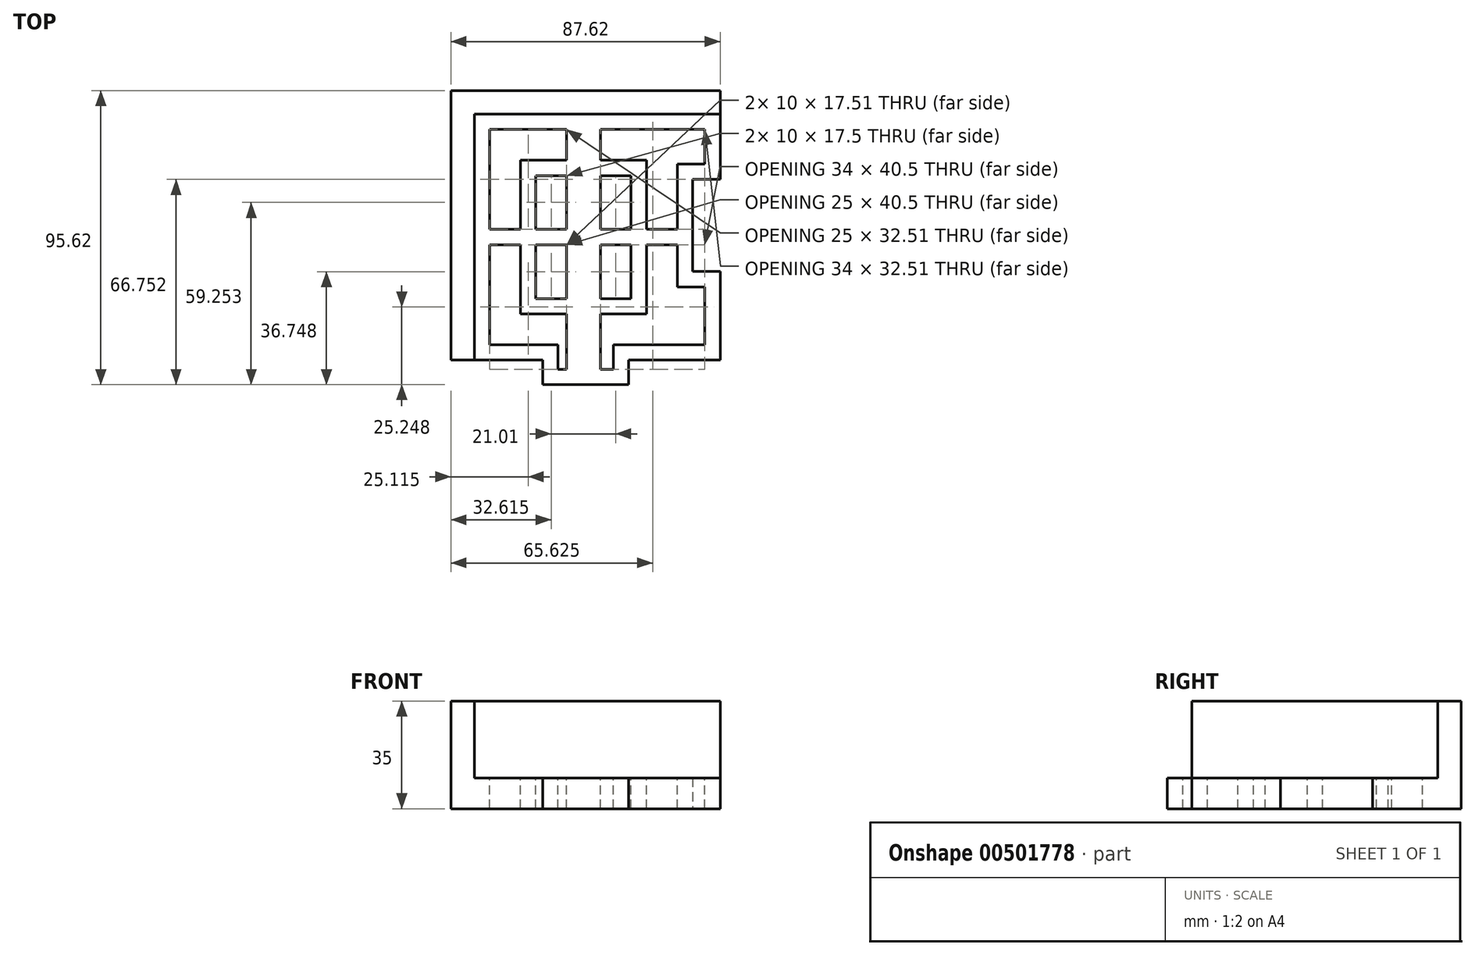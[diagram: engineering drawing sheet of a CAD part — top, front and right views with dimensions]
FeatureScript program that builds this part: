
annotation { "Feature Type Name" : "Feature", "Feature Type Description" : "" }
export const myFeature = defineFeature(function(context is Context, id is Id, definition is map)
    precondition{}
    {
        {
            var Q0;
            Q0=qCreatedBy(makeId("Top.planeOp"),FACE);
            var sketch = newSketch(context, id + "F0", { "sketchPlane" : qUnion([Q0])});
            skLineSegment(sketch, "E0.bottom", {"start": v(43.82, 43.82) * mm, "end": v(-43.81, 43.82) * mm});
            skLineSegment(sketch, "E0.top", {"start": v(43.81, -43.82) * mm, "end": v(-43.81, -43.82) * mm});
            skLineSegment(sketch, "E0.left", {"start": v(43.82, 43.81) * mm, "end": v(43.82, -43.81) * mm});
            skLineSegment(sketch, "E0.right", {"start": v(-43.81, 43.82) * mm, "end": v(-43.81, -43.82) * mm});
            skPoint(sketch, "E0.middle", {"position": v(0, 0) * mm});
            skLineSegment(sketch, "E1.bottom", {"start": v(14, -35.82) * mm, "end": v(-14, -35.82) * mm});
            skLineSegment(sketch, "E1.top", {"start": v(14, -51.82) * mm, "end": v(-14, -51.82) * mm});
            skLineSegment(sketch, "E1.left", {"start": v(14, -35.82) * mm, "end": v(14, -51.82) * mm});
            skLineSegment(sketch, "E1.right", {"start": v(-14, -35.82) * mm, "end": v(-14, -51.82) * mm});
            skPoint(sketch, "E1.middle", {"position": v(0, -43.82) * mm});
            skLineSegment(sketch, "E2.bottom", {"start": v(52.82, 15) * mm, "end": v(34.82, 15) * mm});
            skLineSegment(sketch, "E2.top", {"start": v(52.82, -15) * mm, "end": v(34.82, -15) * mm});
            skLineSegment(sketch, "E2.left", {"start": v(52.82, 15) * mm, "end": v(52.82, -15) * mm});
            skLineSegment(sketch, "E2.right", {"start": v(34.82, 15) * mm, "end": v(34.82, -15) * mm});
            skPoint(sketch, "E2.middle", {"position": v(43.82, 0) * mm});
            skSolve(sketch);
        }
        {
            var Q0;
            {var subQ5=sQuery(id+"F0.wireOp",EDGE,"E1.top");Q0=makeQuery(id+"F0.imprint","IMPRINT",FACE,{"disambiguationData":[TD([[makeQuery(id+"F0.imprint","IMPRINT",EDGE,{"derivedFrom":subQ5}),-1.0]])]});}
            var Q1;
            {var subQ9=sQuery(id+"F0.wireOp",EDGE,"E0.bottom");Q1=makeQuery(id+"F0.imprint","IMPRINT",FACE,{"disambiguationData":[TD([[makeQuery(id+"F0.imprint","IMPRINT",EDGE,{"derivedFrom":subQ9}),1.0]])]});}
            var Q2;
            {var subQ5=sQuery(id+"F0.wireOp",EDGE,"E1.bottom");Q2=makeQuery(id+"F0.imprint","IMPRINT",FACE,{"disambiguationData":[TD([[makeQuery(id+"F0.imprint","IMPRINT",EDGE,{"derivedFrom":subQ5}),1.0]])]});}
            extrude(context, id + "F1", {"entities" : qUnion([Q0, Q1, Q2]), "depth" : 10 * mm});
        }
        {
            var Q0;
            Q0=makeQuery(id+"F1.opExtrude","CAP_FACE",FACE,{"disambiguationData":[OSD([sQuery(id+"F0.wireOp",EDGE,"E0.bottom"),sQuery(id+"F0.wireOp",EDGE,"E0.top"),sQuery(id+"F0.wireOp",EDGE,"E0.left"),sQuery(id+"F0.wireOp",EDGE,"E0.right"),sQuery(id+"F0.wireOp",EDGE,"E1.top"),sQuery(id+"F0.wireOp",EDGE,"E1.left"),sQuery(id+"F0.wireOp",EDGE,"E1.right"),sQuery(id+"F0.wireOp",EDGE,"E2.bottom"),sQuery(id+"F0.wireOp",EDGE,"E2.top"),sQuery(id+"F0.wireOp",EDGE,"E2.right")])],"isStart":false});
            var sketch = newSketch(context, id + "F2", { "sketchPlane" : qUnion([Q0])});
            skLineSegment(sketch, "E3", {"start": v(43.82, 43.82) * mm, "end": v(-43.81, 43.81) * mm});
            skLineSegment(sketch, "E4", {"start": v(-43.81, 43.82) * mm, "end": v(-43.81, -43.82) * mm});
            skLineSegment(sketch, "E5", {"start": v(-43.81, -43.82) * mm, "end": v(-36.2, -43.82) * mm});
            skLineSegment(sketch, "E6", {"start": v(-36.2, -43.82) * mm, "end": v(-36.2, 36.2) * mm});
            skLineSegment(sketch, "E7", {"start": v(-36.2, 36.2) * mm, "end": v(43.82, 36.2) * mm});
            skLineSegment(sketch, "E8", {"start": v(43.82, 36.2) * mm, "end": v(43.82, 43.82) * mm});
            skSolve(sketch);
        }
        {
            var Q0;
            Q0 = qSketchRegion(id + "F2", true);
            extrude(context, id + "F3", {"entities" : qUnion([Q0]), "operationType" : NewBodyOperationType.ADD, "depth" : 25 * mm});
        }
        {
            var Q0;
            Q0=makeQuery(id+"F1.opExtrude","CAP_FACE",FACE,{"disambiguationData":[OSD([sQuery(id+"F0.wireOp",EDGE,"E0.bottom"),sQuery(id+"F0.wireOp",EDGE,"E0.top"),sQuery(id+"F0.wireOp",EDGE,"E0.left"),sQuery(id+"F0.wireOp",EDGE,"E0.right"),sQuery(id+"F0.wireOp",EDGE,"E1.top"),sQuery(id+"F0.wireOp",EDGE,"E1.left"),sQuery(id+"F0.wireOp",EDGE,"E1.right"),sQuery(id+"F0.wireOp",EDGE,"E2.bottom"),sQuery(id+"F0.wireOp",EDGE,"E2.top"),sQuery(id+"F0.wireOp",EDGE,"E2.right")])],"isStart":false});
            var sketch = newSketch(context, id + "F4", { "sketchPlane" : qUnion([Q0])});
            skLineSegment(sketch, "E9.0", {"start": v(38.82, 31.2) * mm, "end": v(-31.2, 31.2) * mm});
            skLineSegment(sketch, "E9.1", {"start": v(9, -46.82) * mm, "end": v(9, -38.82) * mm});
            skLineSegment(sketch, "E9.2", {"start": v(-9, -46.82) * mm, "end": v(9, -46.82) * mm});
            skLineSegment(sketch, "E9.3", {"start": v(-9, -38.82) * mm, "end": v(-9, -46.82) * mm});
            skLineSegment(sketch, "E9.4", {"start": v(-31.2, -38.82) * mm, "end": v(-9, -38.82) * mm});
            skLineSegment(sketch, "E9.5", {"start": v(9, -38.82) * mm, "end": v(38.82, -38.82) * mm});
            skLineSegment(sketch, "E9.6", {"start": v(-31.2, 31.2) * mm, "end": v(-31.2, -38.82) * mm});
            skLineSegment(sketch, "E9.7", {"start": v(38.82, -38.82) * mm, "end": v(38.82, -20) * mm});
            skLineSegment(sketch, "E9.8", {"start": v(38.82, -20) * mm, "end": v(29.82, -20) * mm});
            skLineSegment(sketch, "E9.9", {"start": v(29.82, -20) * mm, "end": v(29.82, 20) * mm});
            skLineSegment(sketch, "E9.10", {"start": v(29.82, 20) * mm, "end": v(38.82, 20) * mm});
            skLineSegment(sketch, "E9.11", {"start": v(38.82, 20) * mm, "end": v(38.82, 31.2) * mm});
            skLineSegment(sketch, "E10.0", {"start": v(-21.2, 21.2) * mm, "end": v(-21.2, -28.82) * mm});
            skLineSegment(sketch, "E10.1", {"start": v(19.82, 21.2) * mm, "end": v(-21.2, 21.2) * mm});
            skLineSegment(sketch, "E10.2", {"start": v(-21.2, -28.82) * mm, "end": v(0.8, -28.82) * mm});
            skLineSegment(sketch, "E10.3", {"start": v(0.8, -28.82) * mm, "end": v(19.82, -28.82) * mm});
            skLineSegment(sketch, "E10.4", {"start": v(19.82, -28.82) * mm, "end": v(19.82, 21.2) * mm});
            skLineSegment(sketch, "E11.0", {"start": v(-16.2, 16.2) * mm, "end": v(-16.2, -23.81) * mm});
            skLineSegment(sketch, "E11.1", {"start": v(14.81, 16.2) * mm, "end": v(-16.2, 16.2) * mm});
            skLineSegment(sketch, "E11.2", {"start": v(-16.2, -23.81) * mm, "end": v(0.8, -23.81) * mm});
            skLineSegment(sketch, "E11.3", {"start": v(0.8, -23.81) * mm, "end": v(14.81, -23.81) * mm});
            skLineSegment(sketch, "E11.4", {"start": v(14.81, -23.81) * mm, "end": v(14.81, 16.2) * mm});
            skLineSegment(sketch, "E12.0", {"start": v(-6.2, 6.2) * mm, "end": v(-6.2, -13.81) * mm});
            skLineSegment(sketch, "E12.1", {"start": v(4.81, 6.2) * mm, "end": v(-6.2, 6.2) * mm});
            skLineSegment(sketch, "E12.2", {"start": v(-6.2, -13.81) * mm, "end": v(0.8, -13.81) * mm});
            skLineSegment(sketch, "E12.3", {"start": v(0.8, -13.81) * mm, "end": v(4.81, -13.81) * mm});
            skLineSegment(sketch, "E12.4", {"start": v(4.81, -13.81) * mm, "end": v(4.81, 6.2) * mm});
            skLineSegment(sketch, "E13.bottom", {"start": v(53.73, -1.31) * mm, "end": v(-53.73, -1.3) * mm});
            skLineSegment(sketch, "E13.top", {"start": v(53.73, -6.31) * mm, "end": v(-53.73, -6.3) * mm});
            skLineSegment(sketch, "E13.left", {"start": v(53.73, -1.31) * mm, "end": v(53.73, -6.31) * mm});
            skLineSegment(sketch, "E13.right", {"start": v(-53.73, -1.3) * mm, "end": v(-53.73, -6.3) * mm});
            skPoint(sketch, "E13.middle", {"position": v(0, -3.81) * mm});
            skPoint(sketch, "E13.middle.positionSnap0", {"position": v(4.81, -3.81) * mm});
            skPoint(sketch, "E13.centerSnap0", {"position": v(4.81, -3.81) * mm});
            skLineSegment(sketch, "E14.bottom", {"start": v(-6.2, 66.16) * mm, "end": v(4.81, 66.16) * mm});
            skLineSegment(sketch, "E14.top", {"start": v(-6.2, -53.77) * mm, "end": v(4.81, -53.77) * mm});
            skLineSegment(sketch, "E14.left", {"start": v(-6.2, 66.16) * mm, "end": v(-6.2, -53.77) * mm});
            skLineSegment(sketch, "E14.right", {"start": v(4.81, 66.16) * mm, "end": v(4.81, -53.77) * mm});
            skPoint(sketch, "E14.middle", {"position": v(-0.69, 6.2) * mm});
            skSolve(sketch);
        }
        {
            var Q0;
            {var subQ7=sQuery(id+"F4.wireOp",EDGE,"E9.6");var subQ8=sQuery(id+"F4.wireOp",EDGE,"E9.0");var subQ9=makeQuery(id+"F4.imprint","INTERSECT",VERTEX,{"derivedFrom":[subQ8,subQ7]});Q0=makeQuery(id+"F4.imprint","IMPRINT",FACE,{"disambiguationData":[TD([[makeQuery(id+"F4.imprint","IMPRINT",EDGE,{"disambiguationData":[TD([[subQ9,1.0]])],"derivedFrom":subQ8}),1.0]])]});}
            var Q1;
            {var subQ1=sQuery(id+"F4.wireOp",EDGE,"E9.10");Q1=makeQuery(id+"F4.imprint","IMPRINT",FACE,{"disambiguationData":[TD([[makeQuery(id+"F4.imprint","IMPRINT",EDGE,{"derivedFrom":subQ1}),1.0]])]});}
            var Q2;
            {var subQ2=sQuery(id+"F4.wireOp",EDGE,"E11.1");var subQ5=sQuery(id+"F4.wireOp",EDGE,"E11.4");var subQ8=makeQuery(id+"F4.imprint","INTERSECT",VERTEX,{"derivedFrom":[subQ2,subQ5]});Q2=makeQuery(id+"F4.imprint","IMPRINT",FACE,{"disambiguationData":[TD([[makeQuery(id+"F4.imprint","IMPRINT",EDGE,{"disambiguationData":[TD([[subQ8,-1.0]])],"derivedFrom":subQ2}),1.0]])]});}
            var Q3;
            {var subQ2=sQuery(id+"F4.wireOp",EDGE,"E11.1");var subQ5=sQuery(id+"F4.wireOp",EDGE,"E11.0");var subQ8=makeQuery(id+"F4.imprint","INTERSECT",VERTEX,{"derivedFrom":[subQ5,subQ2]});Q3=makeQuery(id+"F4.imprint","IMPRINT",FACE,{"disambiguationData":[TD([[makeQuery(id+"F4.imprint","IMPRINT",EDGE,{"disambiguationData":[TD([[subQ8,-1.0]])],"derivedFrom":subQ5}),1.0]])]});}
            var Q4;
            {var subQ4=sQuery(id+"F4.wireOp",EDGE,"E11.0");var subQ6=sQuery(id+"F4.wireOp",EDGE,"E11.2");var subQ7=makeQuery(id+"F4.imprint","INTERSECT",VERTEX,{"derivedFrom":[subQ4,subQ6]});Q4=makeQuery(id+"F4.imprint","IMPRINT",FACE,{"disambiguationData":[TD([[makeQuery(id+"F4.imprint","IMPRINT",EDGE,{"disambiguationData":[TD([[subQ7,1.0]])],"derivedFrom":subQ4}),1.0]])]});}
            var Q5;
            {var subQ9=sQuery(id+"F4.wireOp",EDGE,"E9.3");Q5=makeQuery(id+"F4.imprint","IMPRINT",FACE,{"disambiguationData":[TD([[makeQuery(id+"F4.imprint","IMPRINT",EDGE,{"derivedFrom":subQ9}),1.0]])]});}
            var Q6;
            {var subQ1=sQuery(id+"F4.wireOp",EDGE,"E9.1");Q6=makeQuery(id+"F4.imprint","IMPRINT",FACE,{"disambiguationData":[TD([[makeQuery(id+"F4.imprint","IMPRINT",EDGE,{"derivedFrom":subQ1}),1.0]])]});}
            var Q7;
            {var subQ4=sQuery(id+"F4.wireOp",EDGE,"E11.4");var subQ6=sQuery(id+"F4.wireOp",EDGE,"E11.3");var subQ7=makeQuery(id+"F4.imprint","INTERSECT",VERTEX,{"derivedFrom":[subQ6,subQ4]});Q7=makeQuery(id+"F4.imprint","IMPRINT",FACE,{"disambiguationData":[TD([[makeQuery(id+"F4.imprint","IMPRINT",EDGE,{"disambiguationData":[TD([[subQ7,1.0]])],"derivedFrom":subQ6}),1.0]])]});}
            extrude(context, id + "F5", {"entities" : qUnion([Q0, Q1, Q2, Q3, Q4, Q5, Q6, Q7]), "operationType" : NewBodyOperationType.REMOVE, "endBound" : BoundingType.THROUGH_ALL, "oppositeDirection" : true, "depth" : 25 * mm, "offsetDistance" : 25 * mm});
        }
    });
